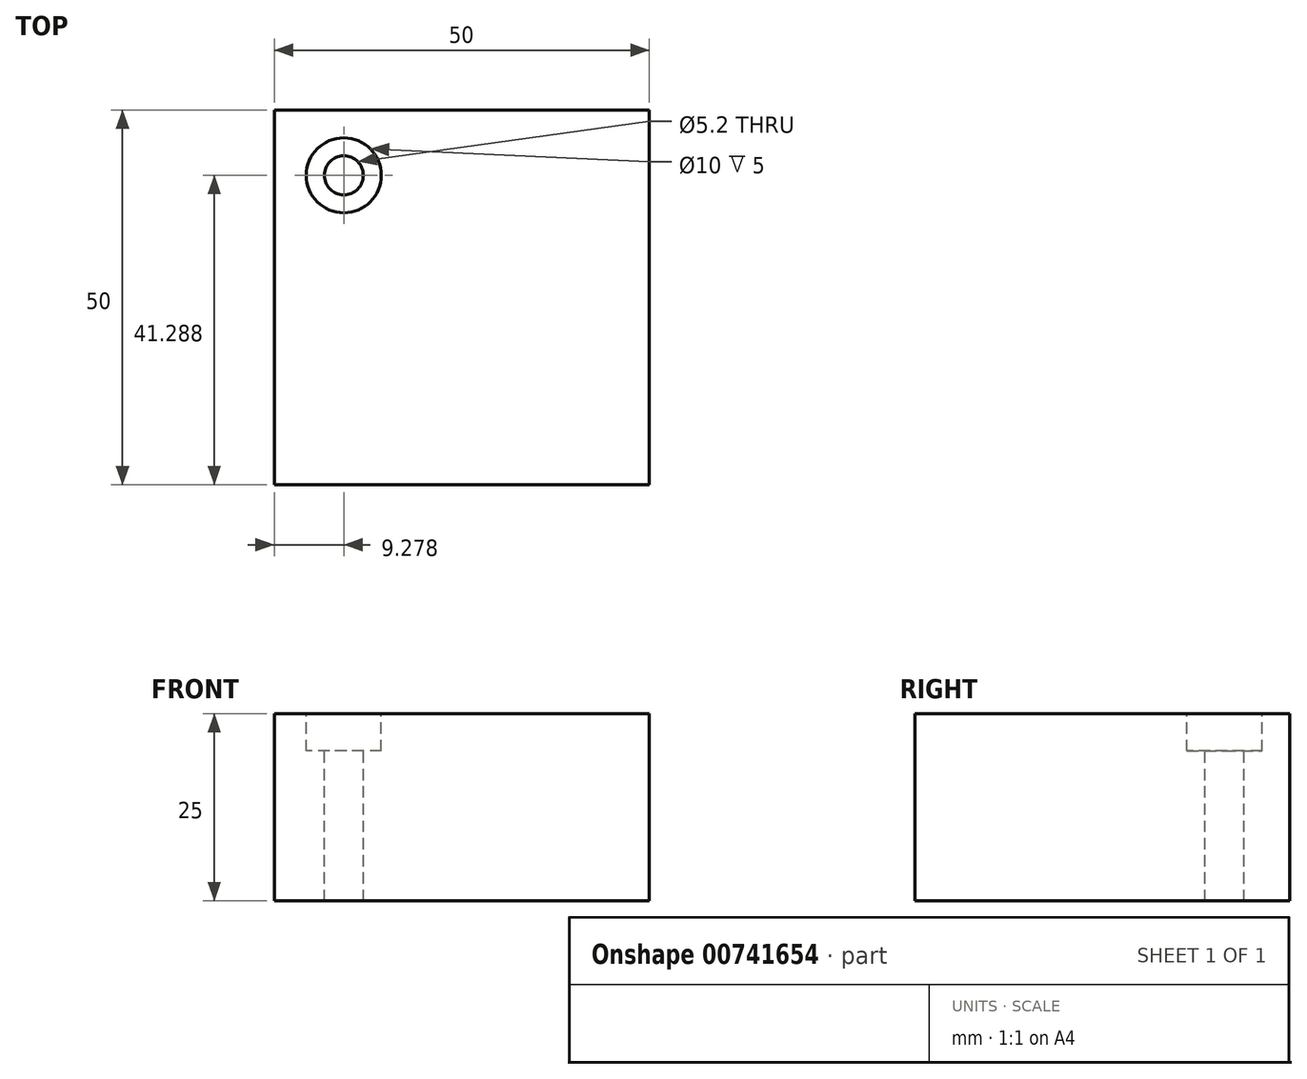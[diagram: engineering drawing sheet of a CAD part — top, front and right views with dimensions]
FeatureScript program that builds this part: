
annotation { "Feature Type Name" : "Feature", "Feature Type Description" : "" }
export const myFeature = defineFeature(function(context is Context, id is Id, definition is map)
    precondition{}
    {
        {
            var Q0;
            Q0=qCreatedBy(makeId("Top.planeOp"),FACE);
            var sketch = newSketch(context, id + "F0", { "sketchPlane" : qUnion([Q0])});
            skLineSegment(sketch, "E0.bottom", {"start": v(25, -25) * mm, "end": v(-25, -25) * mm});
            skLineSegment(sketch, "E0.top", {"start": v(25, 25) * mm, "end": v(-25, 25) * mm});
            skLineSegment(sketch, "E0.left", {"start": v(25, -25) * mm, "end": v(25, 25) * mm});
            skLineSegment(sketch, "E0.right", {"start": v(-25, -25) * mm, "end": v(-25, 25) * mm});
            skPoint(sketch, "E0.middle", {"position": v(0, 0) * mm});
            skSolve(sketch);
        }
        {
            var Q0;
            Q0=makeQuery(id+"F0.imprint","IMPRINT",FACE,{"disambiguationData":[TD([[makeQuery(id+"F0.imprint","IMPRINT",EDGE,{"derivedFrom":sQuery(id+"F0.wireOp",EDGE,"E0.bottom")}),-1.0]])]});
            extrude(context, id + "F1", {"entities" : qUnion([Q0]), "oppositeDirection" : true, "depth" : 25 * mm, "offsetDistance" : 25 * mm});
        }
        {
            var Q0;
            Q0=makeQuery(id+"F1.opExtrude","CAP_FACE",FACE,{"disambiguationData":[OSD([sQuery(id+"F0.wireOp",EDGE,"E0.bottom"),sQuery(id+"F0.wireOp",EDGE,"E0.top"),sQuery(id+"F0.wireOp",EDGE,"E0.left"),sQuery(id+"F0.wireOp",EDGE,"E0.right")])],"isStart":true});
            var sketch = newSketch(context, id + "F2", { "sketchPlane" : qUnion([Q0])});
            skPoint(sketch, "E1", {"position": v(-15.72, 16.29) * mm});
            skSolve(sketch);
        }
        {
            var Q0;
            Q0=sQuery(id+"F2.wireOp",VERTEX,"E1");
            var Q1;
            Q1=makeQuery(id+"F1.opExtrude","SWEPT_BODY",BODY,{"disambiguationData":[OSD([sQuery(id+"F0.wireOp",EDGE,"E0.bottom"),sQuery(id+"F0.wireOp",EDGE,"E0.top"),sQuery(id+"F0.wireOp",EDGE,"E0.left"),sQuery(id+"F0.wireOp",EDGE,"E0.right")])]});
            hole(context, id + "F3", {"style" : HoleStyle.C_BORE, "endStyle" : HoleEndStyle.THROUGH, "holeDiameter" : 5.2 * mm, "cBoreDiameter" : 10 * mm, "cBoreDepth" : 5 * mm, "majorDiameter" : 5 * mm, "isTappedThrough" : true, "tappedDepth" : 12 * mm, "tapClearance" : 3, "startFromSketch" : true, "locations" : qUnion([Q0]), "scope" : qUnion([Q1])});
        }
    });
